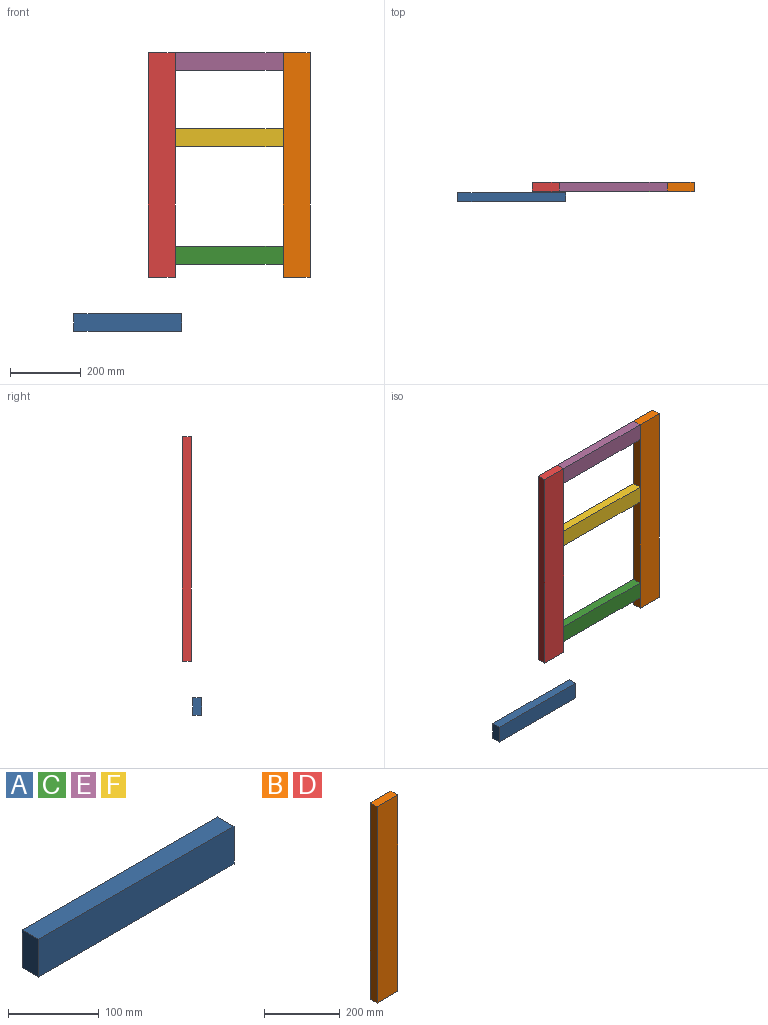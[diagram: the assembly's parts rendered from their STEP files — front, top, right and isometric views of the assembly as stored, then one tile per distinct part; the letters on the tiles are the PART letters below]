
ASSEMBLY  parts=6 mates=8
PART A: 6 faces, bbox 304.8x25.4x50.8 mm
  f0: plane 304.8x25.4mm, normal (0,0,-1), area 7741.9mm2, adj f1,f3,f4,f5
  f1: plane 304.8x50.8mm, normal (0,1,0), area 15483.8mm2, adj f0,f2,f4,f5
  f2: plane 304.8x25.4mm, normal (0,0,1), area 7741.9mm2, adj f1,f3,f4,f5
  f3: plane 304.8x50.8mm, normal (0,-1,0), area 15483.8mm2, adj f0,f2,f4,f5
  f4: plane 50.8x25.4mm, normal (1,0,0), area 1290.3mm2, adj f0,f1,f2,f3
  f5: plane 50.8x25.4mm, normal (-1,0,0), area 1290.3mm2, adj f0,f1,f2,f3
PART B: 6 faces, bbox 76.2x25.4x635 mm
  f0: plane 635x25.4mm, normal (-1,0,0), area 16129mm2, adj f1,f3,f4,f5
  f1: plane 635x76.2mm, normal (0,-1,0), area 48387mm2, adj f0,f2,f4,f5
  f2: plane 635x25.4mm, normal (1,0,0), area 16129mm2, adj f1,f3,f4,f5
  f3: plane 635x76.2mm, normal (0,1,0), area 48387mm2, adj f0,f2,f4,f5
  f4: plane 76.2x25.4mm, normal (0,0,1), area 1935.5mm2, adj f0,f1,f2,f3
  f5: plane 76.2x25.4mm, normal (0,0,-1), area 1935.5mm2, adj f0,f1,f2,f3
PART C: same geometry as A
PART D: same geometry as B
PART E: same geometry as A
PART F: same geometry as A
PLACE A t=(-286.48,-3.01,-153.3)mm
PLACE B t=(304.8,0,0)mm
PLACE C t=(0,25.4,36.64)mm
PLACE D t=(-76.2,0,0)mm
PLACE E t=(0,25.4,584.2)mm
PLACE F t=(0,25.4,368.07)mm
MATE planar F.f5 <-> D.f2  axis (-1,0,0) through (0,12.7,393.47)mm
MATE planar F.f3 <-> D.f1  axis (0,-1,0) through (152.4,0,393.47)mm
MATE planar C.f3 <-> D.f1  axis (0,-1,0) through (152.4,0,62.04)mm
MATE parallel C.f0 <-> D.f5  axis (0,0,-1) through (152.4,12.7,36.64)mm
MATE fastened B.f4 <-> E.f2  axis (0,0,-1) through (304.8,0,635)mm
MATE planar C.f5 <-> D.f2  axis (-1,0,0) through (0,12.7,62.04)mm
MATE fastened D.f1 <-> E.f3  axis (0,-1,0) through (0,0,635)mm
MATE planar E.f1 <-> D.f3  axis (0,1,0) through (0,25.4,584.2)mm
